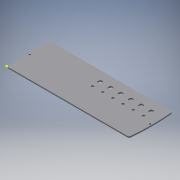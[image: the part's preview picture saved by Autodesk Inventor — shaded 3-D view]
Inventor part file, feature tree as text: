
AUTODESK INVENTOR PART (.ipt)
format: ipt  version: 2018 (Build 220112000, 112)  size: 185,344 bytes
history: native  units: mm
features: sketch x5, extrude x3, hole x1
ambient origin geometry x8: Origin, YZ Plane, XZ Plane, XY Plane, X Axis, Y Axis, Z Axis, Center Point
bodies: Volumenkörper1 (feature_tree)
feature tree (9):
  extrude  "Extrusion1"  Depth=85.0mm
  hole  "Bohrung1"  [1 undecoded]
  extrude  "Extrusion2"  Depth=2.0mm
  sketch  "Sketch7"  dims[d7=452.5625mm d8=452.5625mm]
  extrude  "Extrusion6"  Depth=452.5625mm
  sketch  "Skizze1"  dims[d0=85.0mm d1=242.0mm]
  sketch  "Skizze2"  dims[d2=2.0mm d3=2.0mm]
  sketch  "Skizze3"  dims[d4=2.0mm d5=905.125mm d6=905.125mm]
  sketch  "Sketch9"  dims[d9=2.5mm d10=0.0mm d11=42.5mm d12=42.5mm d13=235.8mm d14=117.9mm d15=117.9mm d16=3.3mm d17=6.0mm d18=4.0mm d19=2.0mm d20=90.0deg d21=8.0mm d22=20.594885mm d23=9.599311mm d24=9.599311mm d25=2.5mm d26=2.5mm d27=5.0mm d28=0.0mm d96=8.1mm d97=20.0mm d98=20.0mm d99=7.1mm d100=4.05mm d101=60.0mm d103=20.0mm d104=10.0mm d106=10.0mm d108=15.0mm d109=4.8mm d110=60.0mm d112=20.0mm d113=10.0mm d115=10.0mm d117=3.0mm d118=0.0mm]
note: 1 required parameter value undecoded (feature->parameter linkage not recoverable at this tier; creation-order binding heuristic only, values carry confidence <= 0.55)
